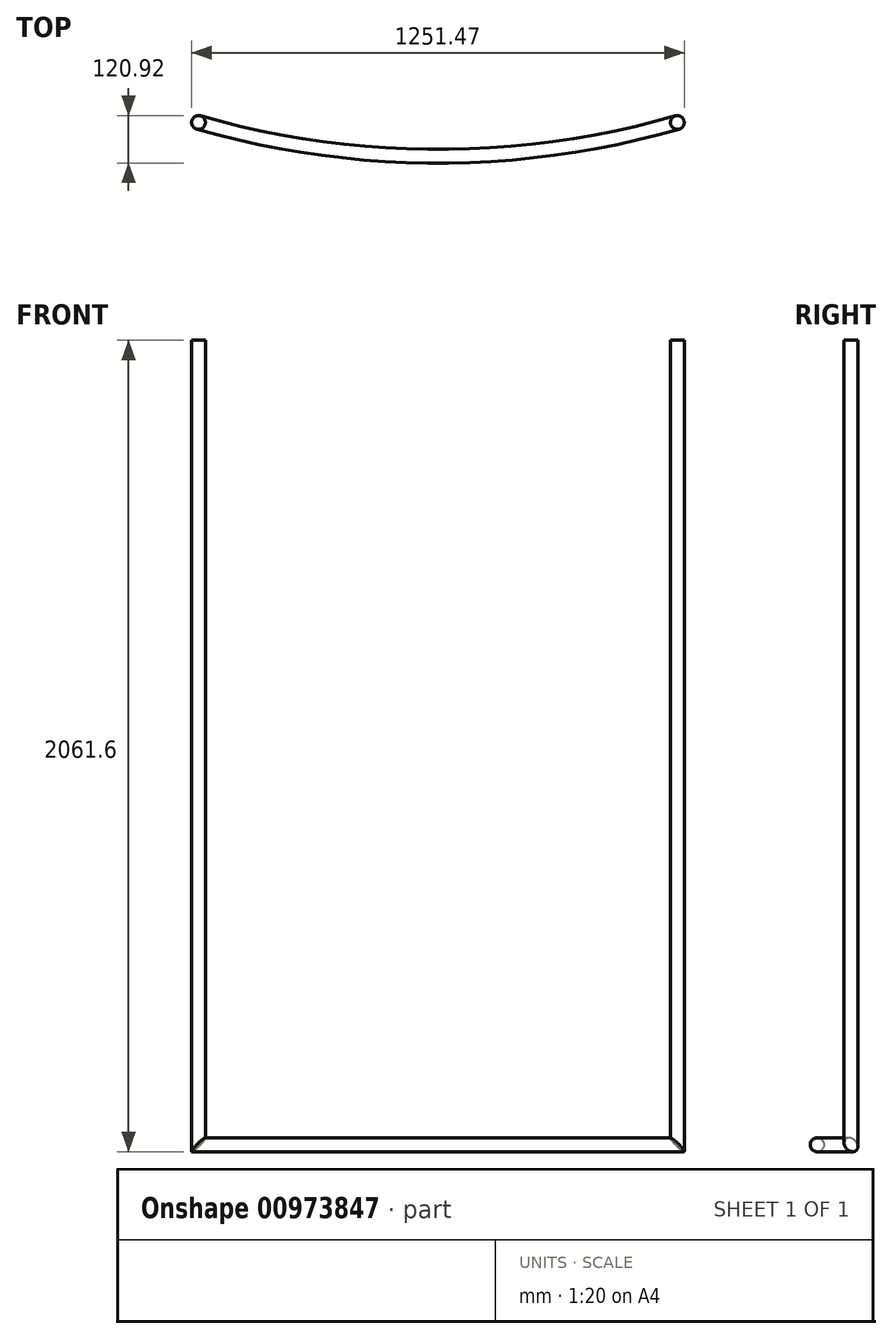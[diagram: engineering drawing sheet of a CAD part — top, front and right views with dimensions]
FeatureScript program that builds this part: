
annotation { "Feature Type Name" : "Feature", "Feature Type Description" : "" }
export const myFeature = defineFeature(function(context is Context, id is Id, definition is map)
    precondition{}
    {
        {
            var Q0;
            Q0=qCreatedBy(makeId("Top.planeOp"),FACE);
            var sketch = newSketch(context, id + "F0", { "sketchPlane" : qUnion([Q0])});
            skCircle(sketch, "E0", {"center": v(0, 0) * mm, "radius": 17.49 * mm});
            skSolve(sketch);
        }
        {
            var Q0;
            Q0=qCreatedBy(makeId("Top.planeOp"),FACE);
            var sketch = newSketch(context, id + "F1", { "sketchPlane" : qUnion([Q0])});
            skArc(sketch, "E1", {"start": v(0, 0) * mm, "mid": v(608.25, -85.94) * mm, "end": v(1216.5, 0) * mm});
            skSolve(sketch);
        }
        {
            var Q0;
            Q0=qCreatedBy(makeId("Front.planeOp"),FACE);
            var sketch = newSketch(context, id + "F2", { "sketchPlane" : qUnion([Q0])});
            skLineSegment(sketch, "E2.left", {"start": v(0, 0) * mm, "end": v(0, 2044.1) * mm});
            skLineSegment(sketch, "E2.right", {"start": v(1216.5, 0) * mm, "end": v(1216.5, 2044.1) * mm});
            skSolve(sketch);
        }
        {
            var Q0;
            Q0=makeQuery(id+"F0.imprint","IMPRINT",FACE,{"disambiguationData":[TD([[makeQuery(id+"F0.imprint","IMPRINT",EDGE,{"derivedFrom":sQuery(id+"F0.wireOp",EDGE,"E0")}),1.0]])]});
            var Q1;
            Q1=sQuery(id+"F2.wireOp",EDGE,"E2.left");
            var Q2;
            Q2=sQuery(id+"F2.wireOp",EDGE,"E2.right");
            var Q3;
            Q3=sQuery(id+"F1.wireOp",EDGE,"E1");
            sweep(context, id + "F3", {"profiles" : qUnion([Q0]), "path" : qUnion([Q1, Q2, Q3])});
        }
    });
